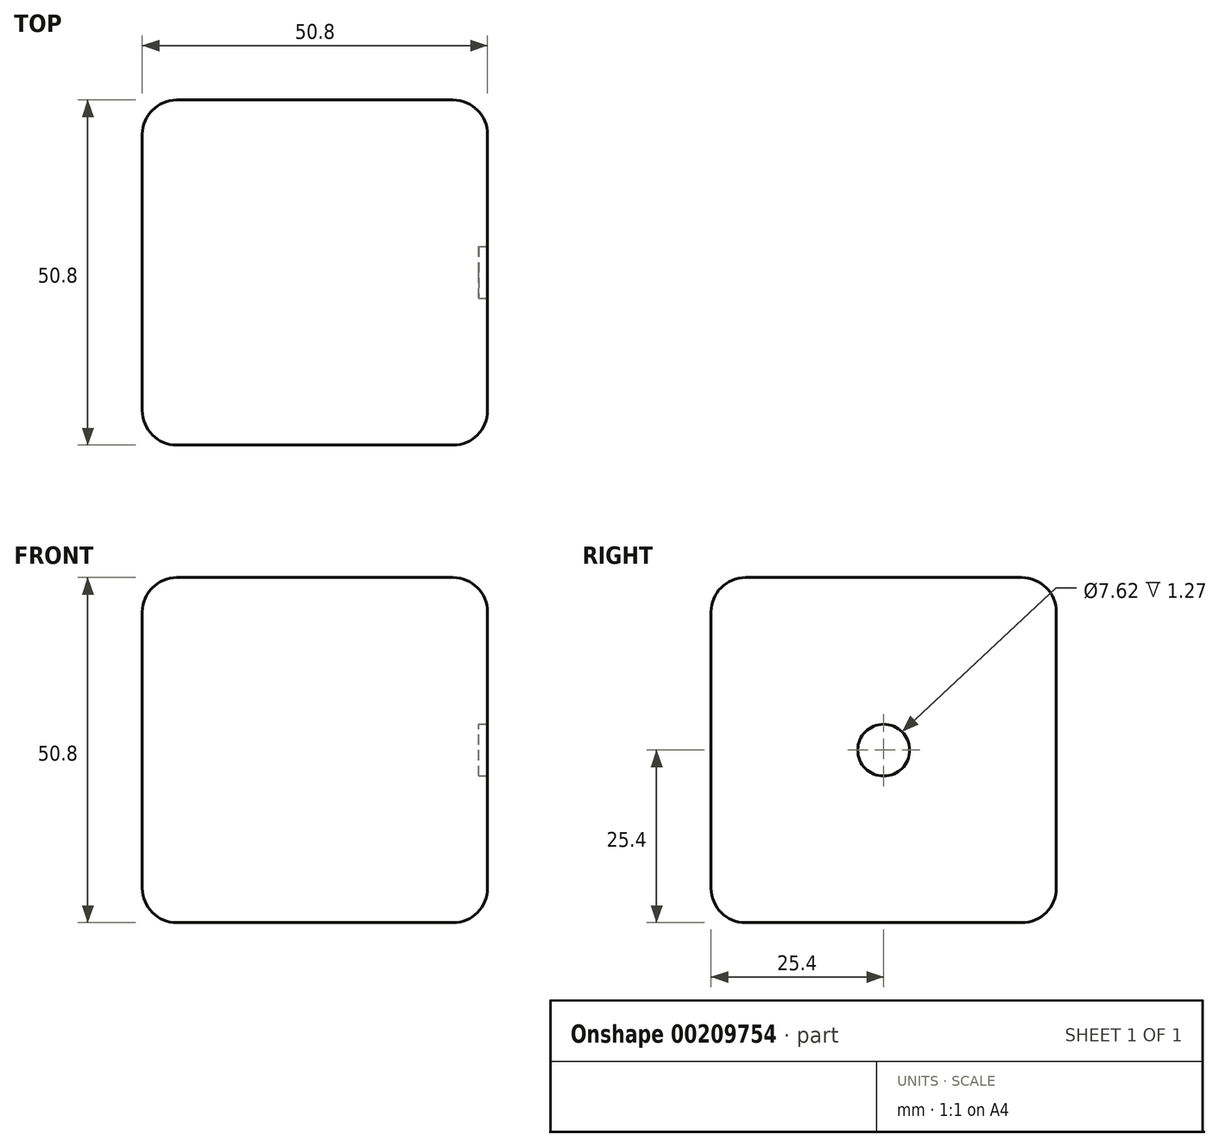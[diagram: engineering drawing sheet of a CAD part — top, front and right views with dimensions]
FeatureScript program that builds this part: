
annotation { "Feature Type Name" : "Feature", "Feature Type Description" : "" }
export const myFeature = defineFeature(function(context is Context, id is Id, definition is map)
    precondition{}
    {
        {
            var Q0;
            Q0=qCreatedBy(makeId("Front.planeOp"),FACE);
            var sketch = newSketch(context, id + "F0", { "sketchPlane" : qUnion([Q0])});
            skLineSegment(sketch, "E0.bottom", {"start": v(0, 0) * mm, "end": v(50.8, 0) * mm});
            skLineSegment(sketch, "E0.top", {"start": v(0, 50.8) * mm, "end": v(50.8, 50.8) * mm});
            skLineSegment(sketch, "E0.left", {"start": v(0, 0) * mm, "end": v(0, 50.8) * mm});
            skLineSegment(sketch, "E0.right", {"start": v(50.8, 0) * mm, "end": v(50.8, 50.8) * mm});
            skSolve(sketch);
        }
        {
            var Q0;
            Q0=makeQuery(id+"F0.imprint","IMPRINT",FACE,{"disambiguationData":[TD([[makeQuery(id+"F0.imprint","IMPRINT",EDGE,{"derivedFrom":sQuery(id+"F0.wireOp",EDGE,"E0.bottom")}),1.0]])]});
            extrude(context, id + "F1", {"entities" : qUnion([Q0]), "depth" : 50.8 * mm});
        }
        {
            var Q0;
            Q0=makeQuery(id+"F1.opExtrude","CAP_EDGE",EDGE,{"disambiguationData":[OSD([sQuery(id+"F0.wireOp",EDGE,"E0.top")])],"isStart":false});
            fillet(context, id + "F2", {"entities" : qUnion([Q0]), "radius" : 5.08 * mm, "tangentPropagation" : true, "allowEdgeOverflow" : false});
        }
        {
            var Q0;
            Q0=makeQuery(id+"F1.opExtrude","CAP_EDGE",EDGE,{"disambiguationData":[OSD([sQuery(id+"F0.wireOp",EDGE,"E0.top")])],"isStart":true});
            var Q1;
            Q1=makeQuery(id+"F1.opExtrude","CAP_FACE",FACE,{"disambiguationData":[OSD([sQuery(id+"F0.wireOp",EDGE,"E0.bottom"),sQuery(id+"F0.wireOp",EDGE,"E0.top"),sQuery(id+"F0.wireOp",EDGE,"E0.left"),sQuery(id+"F0.wireOp",EDGE,"E0.right")])],"isStart":true});
            fillet(context, id + "F3", {"entities" : qUnion([Q0, Q1]), "radius" : 5.08 * mm, "tangentPropagation" : true, "allowEdgeOverflow" : false});
        }
        {
            var Q0;
            Q0=makeQuery(id+"F1.opExtrude","CAP_FACE",FACE,{"disambiguationData":[OSD([sQuery(id+"F0.wireOp",EDGE,"E0.bottom"),sQuery(id+"F0.wireOp",EDGE,"E0.top"),sQuery(id+"F0.wireOp",EDGE,"E0.left"),sQuery(id+"F0.wireOp",EDGE,"E0.right")])],"isStart":false});
            fillet(context, id + "F4", {"entities" : qUnion([Q0]), "radius" : 5.08 * mm, "tangentPropagation" : true, "allowEdgeOverflow" : false});
        }
        {
            var Q0;
            Q0=makeQuery(id+"F1.opExtrude","SWEPT_FACE",FACE,{"disambiguationData":[OSD([sQuery(id+"F0.wireOp",EDGE,"E0.left")])]});
            fillet(context, id + "F5", {"entities" : qUnion([Q0]), "radius" : 5.08 * mm, "tangentPropagation" : true, "allowEdgeOverflow" : false});
        }
        {
            var Q0;
            Q0=makeQuery(id+"F1.opExtrude","SWEPT_FACE",FACE,{"disambiguationData":[OSD([sQuery(id+"F0.wireOp",EDGE,"E0.bottom")])]});
            fillet(context, id + "F6", {"entities" : qUnion([Q0]), "radius" : 5.08 * mm, "tangentPropagation" : true, "allowEdgeOverflow" : false});
        }
        {
            var Q0;
            Q0=makeQuery(id+"F1.opExtrude","SWEPT_FACE",FACE,{"disambiguationData":[OSD([sQuery(id+"F0.wireOp",EDGE,"E0.right")])]});
            var sketch = newSketch(context, id + "F7", { "sketchPlane" : qUnion([Q0])});
            skCircle(sketch, "E1", {"center": v(-25.4, 25.4) * mm, "radius": 3.81 * mm});
            skSolve(sketch);
        }
        {
            var Q0;
            Q0=makeQuery(id+"F7.imprint","IMPRINT",FACE,{"disambiguationData":[TD([[makeQuery(id+"F7.imprint","IMPRINT",EDGE,{"derivedFrom":sQuery(id+"F7.wireOp",EDGE,"E1")}),1.0]])]});
            extrude(context, id + "F8", {"entities" : qUnion([Q0]), "operationType" : NewBodyOperationType.REMOVE, "oppositeDirection" : true, "depth" : 1.27 * mm});
        }
    });
